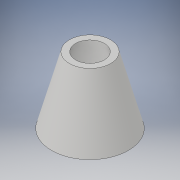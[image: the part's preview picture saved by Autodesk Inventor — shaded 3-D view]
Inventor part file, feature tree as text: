
AUTODESK INVENTOR PART (.ipt)
format: ipt  version: 2018 (Build 220112000, 112)  size: 124,416 bytes
history: native  units: in
note: dims shown in document units (in); Inventor stores cm internally (conversion verified against a paired STEP export)
features: revolve x1, sketch x1
ambient origin geometry x8: Origin, YZ Plane, XZ Plane, XY Plane, X Axis, Y Axis, Z Axis, Center Point
bodies: Solid1 (feature_tree)
feature tree (2):
  revolve  "Revolution1"  Angle=75.0deg
  sketch  "Sketch1"  dims[d0=72.8346in d5=75.0deg d6=11.811in d7=0.0in d8=90.0deg]
